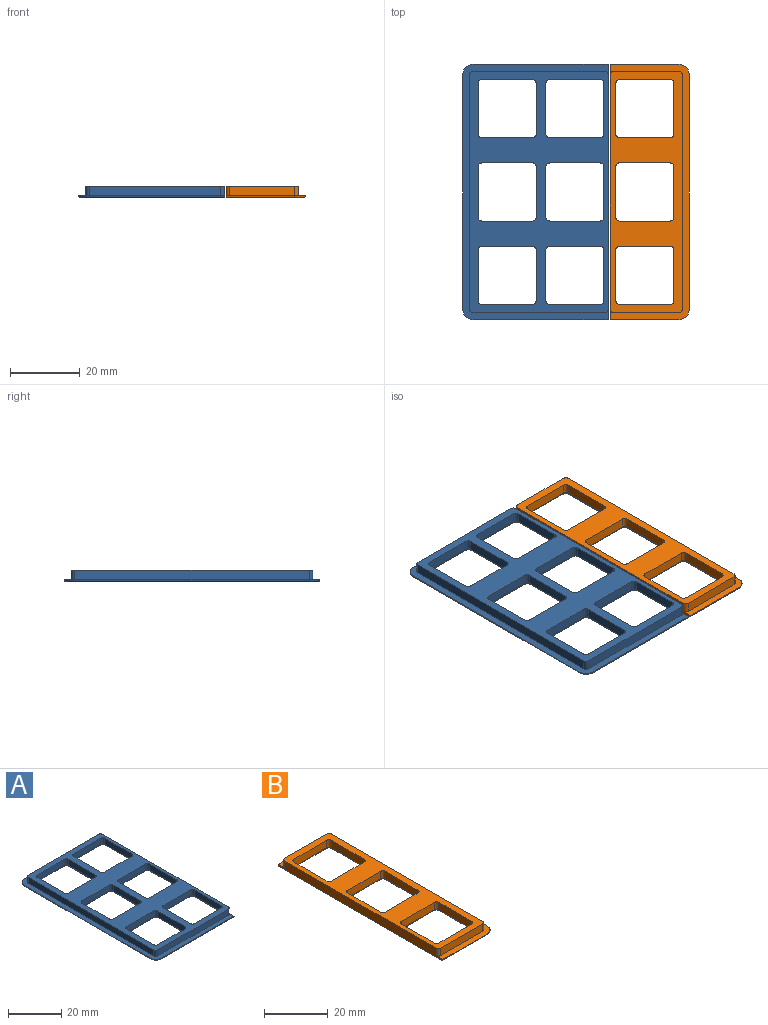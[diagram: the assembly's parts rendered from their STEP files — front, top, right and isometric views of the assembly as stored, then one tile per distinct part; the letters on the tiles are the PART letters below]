
ASSEMBLY  parts=2 mates=1
PART A: 112 faces, bbox 41.8x73.5x3.4 mm
  f0: plane 73x3.4mm, normal (1,0,0), area 231.2mm2, adj f1,f2,f30,f56,f57,f107,f111
  f1: plane 73x41.6mm, normal (0,0,1), area 301.4mm2, adj f0,f3,f4,f29,f55,f56,f57,f58
  f2: plane 71.8x41mm, normal (0,0,-1), area 1053.5mm2, adj f0,f59,f60,f61,f62,f63,f64,f65
  f3: plane 67x2.8mm, normal (-1,0,0), area 187.6mm2, adj f1,f30,f55,f58
  f4: plane 37.6x2.8mm, normal (0,-1,0), area 105.3mm2, adj f1,f30,f55,f56
  f5: plane 14.6x2.8mm, normal (1,0,0), area 40.9mm2, adj f30,f51,f54,f59
  f6: plane 14.6x2.8mm, normal (0,-1,0), area 40.9mm2, adj f30,f51,f52,f62
  f7: plane 14.6x2.8mm, normal (-1,0,0), area 40.9mm2, adj f30,f52,f53,f66
  f8: plane 14.6x2.8mm, normal (1,0,0), area 40.9mm2, adj f30,f47,f50,f67
  f9: plane 14.6x2.8mm, normal (0,-1,0), area 40.9mm2, adj f30,f47,f48,f70
  f10: plane 14.6x2.8mm, normal (-1,0,0), area 40.9mm2, adj f30,f48,f49,f74
  f11: plane 14.6x2.8mm, normal (1,0,0), area 40.9mm2, adj f30,f43,f46,f75
  f12: plane 14.6x2.8mm, normal (0,-1,0), area 40.9mm2, adj f30,f43,f44,f78
  f13: plane 14.6x2.8mm, normal (-1,0,0), area 40.9mm2, adj f30,f44,f45,f82
  f14: plane 14.6x2.8mm, normal (1,0,0), area 40.9mm2, adj f30,f39,f42,f83
  f15: plane 14.6x2.8mm, normal (0,-1,0), area 40.9mm2, adj f30,f39,f40,f86
  f16: plane 14.6x2.8mm, normal (-1,0,0), area 40.9mm2, adj f30,f40,f41,f90
  f17: plane 14.6x2.8mm, normal (1,0,0), area 40.9mm2, adj f30,f35,f38,f91
  f18: plane 14.6x2.8mm, normal (0,-1,0), area 40.9mm2, adj f30,f35,f36,f94
  f19: plane 14.6x2.8mm, normal (-1,0,0), area 40.9mm2, adj f30,f36,f37,f98
  f20: plane 14.6x2.8mm, normal (1,0,0), area 40.9mm2, adj f30,f31,f34,f99
  f21: plane 14.6x2.8mm, normal (0,-1,0), area 40.9mm2, adj f30,f31,f32,f102
  f22: plane 14.6x2.8mm, normal (-1,0,0), area 40.9mm2, adj f30,f32,f33,f106
  f23: plane 14.6x2.8mm, normal (0,1,0), area 40.9mm2, adj f30,f53,f54,f63
  f24: plane 14.6x2.8mm, normal (0,1,0), area 40.9mm2, adj f30,f49,f50,f71
  f25: plane 14.6x2.8mm, normal (0,1,0), area 40.9mm2, adj f30,f45,f46,f79
  f26: plane 14.6x2.8mm, normal (0,1,0), area 40.9mm2, adj f30,f41,f42,f87
  f27: plane 14.6x2.8mm, normal (0,1,0), area 40.9mm2, adj f30,f37,f38,f95
  f28: plane 14.6x2.8mm, normal (0,1,0), area 40.9mm2, adj f30,f33,f34,f103
  f29: plane 37.6x2.8mm, normal (0,1,0), area 105.3mm2, adj f1,f30,f57,f58
  f30: plane 69x39.6mm, normal (0,0,1), area 1083.3mm2, adj f0,f3,f4,f5,f6,f7,f8,f9
  f31: cylinder r=1mm len=2.8mm, axis (0,0,-1), area 4.4mm2, adj f20,f21,f30,f100
  f32: cylinder r=1mm len=2.8mm, axis (0,0,1), area 4.4mm2, adj f21,f22,f30,f104
  f33: cylinder r=1mm len=2.8mm, axis (0,0,-1), area 4.4mm2, adj f22,f28,f30,f105
  f34: cylinder r=1mm len=2.8mm, axis (0,0,1), area 4.4mm2, adj f20,f28,f30,f101
  f35: cylinder r=1mm len=2.8mm, axis (0,0,-1), area 4.4mm2, adj f17,f18,f30,f92
  f36: cylinder r=1mm len=2.8mm, axis (0,0,1), area 4.4mm2, adj f18,f19,f30,f96
  f37: cylinder r=1mm len=2.8mm, axis (0,0,-1), area 4.4mm2, adj f19,f27,f30,f97
  f38: cylinder r=1mm len=2.8mm, axis (0,0,1), area 4.4mm2, adj f17,f27,f30,f93
  f39: cylinder r=1mm len=2.8mm, axis (0,0,-1), area 4.4mm2, adj f14,f15,f30,f84
  f40: cylinder r=1mm len=2.8mm, axis (0,0,1), area 4.4mm2, adj f15,f16,f30,f88
  f41: cylinder r=1mm len=2.8mm, axis (0,0,-1), area 4.4mm2, adj f16,f26,f30,f89
  f42: cylinder r=1mm len=2.8mm, axis (0,0,1), area 4.4mm2, adj f14,f26,f30,f85
  f43: cylinder r=1mm len=2.8mm, axis (0,0,-1), area 4.4mm2, adj f11,f12,f30,f76
  f44: cylinder r=1mm len=2.8mm, axis (0,0,1), area 4.4mm2, adj f12,f13,f30,f80
  f45: cylinder r=1mm len=2.8mm, axis (0,0,-1), area 4.4mm2, adj f13,f25,f30,f81
  f46: cylinder r=1mm len=2.8mm, axis (0,0,1), area 4.4mm2, adj f11,f25,f30,f77
  f47: cylinder r=1mm len=2.8mm, axis (0,0,-1), area 4.4mm2, adj f8,f9,f30,f68
  f48: cylinder r=1mm len=2.8mm, axis (0,0,1), area 4.4mm2, adj f9,f10,f30,f72
  f49: cylinder r=1mm len=2.8mm, axis (0,0,-1), area 4.4mm2, adj f10,f24,f30,f73
  f50: cylinder r=1mm len=2.8mm, axis (0,0,1), area 4.4mm2, adj f8,f24,f30,f69
  f51: cylinder r=1mm len=2.8mm, axis (0,0,-1), area 4.4mm2, adj f5,f6,f30,f60
  f52: cylinder r=1mm len=2.8mm, axis (0,0,1), area 4.4mm2, adj f6,f7,f30,f64
  f53: cylinder r=1mm len=2.8mm, axis (0,0,-1), area 4.4mm2, adj f7,f23,f30,f65
  f54: cylinder r=1mm len=2.8mm, axis (0,0,1), area 4.4mm2, adj f5,f23,f30,f61
  f55: cylinder r=1mm len=2.8mm, axis (0,0,-1), area 4.4mm2, adj f1,f3,f4,f30
  f56: cylinder r=1mm len=2.8mm, axis (0,0,-1), area 4.4mm2, adj f0,f1,f4,f30
  f57: cylinder r=1mm len=2.8mm, axis (0,0,1), area 4.4mm2, adj f0,f1,f29,f30
  f58: cylinder r=1mm len=2.8mm, axis (0,0,1), area 4.4mm2, adj f1,f3,f29,f30
  f59: cylinder r=0.6mm len=14.6mm, axis (0,1,0), area 13.8mm2, adj f2,f5,f60,f61
  f60: torus R=1.6mm, axis (0,0,1), area 1.8mm2, adj f2,f51,f59,f62
  f61: torus R=1.6mm, axis (0,0,1), area 1.8mm2, adj f2,f54,f59,f63
  f62: cylinder r=0.6mm len=14.6mm, axis (1,0,0), area 13.8mm2, adj f2,f6,f60,f64
  f63: cylinder r=0.6mm len=14.6mm, axis (-1,0,0), area 13.8mm2, adj f2,f23,f61,f65
  f64: torus R=1.6mm, axis (0,0,1), area 1.8mm2, adj f2,f52,f62,f66
  f65: torus R=1.6mm, axis (0,0,1), area 1.8mm2, adj f2,f53,f63,f66
  f66: cylinder r=0.6mm len=14.6mm, axis (0,-1,0), area 13.8mm2, adj f2,f7,f64,f65
  f67: cylinder r=0.6mm len=14.6mm, axis (0,1,0), area 13.8mm2, adj f2,f8,f68,f69
  f68: torus R=1.6mm, axis (0,0,1), area 1.8mm2, adj f2,f47,f67,f70
  f69: torus R=1.6mm, axis (0,0,1), area 1.8mm2, adj f2,f50,f67,f71
  f70: cylinder r=0.6mm len=14.6mm, axis (1,0,0), area 13.8mm2, adj f2,f9,f68,f72
  f71: cylinder r=0.6mm len=14.6mm, axis (-1,0,0), area 13.8mm2, adj f2,f24,f69,f73
  f72: torus R=1.6mm, axis (0,0,1), area 1.8mm2, adj f2,f48,f70,f74
  f73: torus R=1.6mm, axis (0,0,1), area 1.8mm2, adj f2,f49,f71,f74
  f74: cylinder r=0.6mm len=14.6mm, axis (0,-1,0), area 13.8mm2, adj f2,f10,f72,f73
  f75: cylinder r=0.6mm len=14.6mm, axis (0,1,0), area 13.8mm2, adj f2,f11,f76,f77
  f76: torus R=1.6mm, axis (0,0,1), area 1.8mm2, adj f2,f43,f75,f78
  f77: torus R=1.6mm, axis (0,0,1), area 1.8mm2, adj f2,f46,f75,f79
  f78: cylinder r=0.6mm len=14.6mm, axis (1,0,0), area 13.8mm2, adj f2,f12,f76,f80
  f79: cylinder r=0.6mm len=14.6mm, axis (-1,0,0), area 13.8mm2, adj f2,f25,f77,f81
  f80: torus R=1.6mm, axis (0,0,1), area 1.8mm2, adj f2,f44,f78,f82
  f81: torus R=1.6mm, axis (0,0,1), area 1.8mm2, adj f2,f45,f79,f82
  f82: cylinder r=0.6mm len=14.6mm, axis (0,-1,0), area 13.8mm2, adj f2,f13,f80,f81
  f83: cylinder r=0.6mm len=14.6mm, axis (0,1,0), area 13.8mm2, adj f2,f14,f84,f85
  f84: torus R=1.6mm, axis (0,0,1), area 1.8mm2, adj f2,f39,f83,f86
  f85: torus R=1.6mm, axis (0,0,1), area 1.8mm2, adj f2,f42,f83,f87
  f86: cylinder r=0.6mm len=14.6mm, axis (1,0,0), area 13.8mm2, adj f2,f15,f84,f88
  f87: cylinder r=0.6mm len=14.6mm, axis (-1,0,0), area 13.8mm2, adj f2,f26,f85,f89
  f88: torus R=1.6mm, axis (0,0,1), area 1.8mm2, adj f2,f40,f86,f90
  f89: torus R=1.6mm, axis (0,0,1), area 1.8mm2, adj f2,f41,f87,f90
  f90: cylinder r=0.6mm len=14.6mm, axis (0,-1,0), area 13.8mm2, adj f2,f16,f88,f89
  f91: cylinder r=0.6mm len=14.6mm, axis (0,1,0), area 13.8mm2, adj f2,f17,f92,f93
  f92: torus R=1.6mm, axis (0,0,1), area 1.8mm2, adj f2,f35,f91,f94
  f93: torus R=1.6mm, axis (0,0,1), area 1.8mm2, adj f2,f38,f91,f95
  f94: cylinder r=0.6mm len=14.6mm, axis (1,0,0), area 13.8mm2, adj f2,f18,f92,f96
  f95: cylinder r=0.6mm len=14.6mm, axis (-1,0,0), area 13.8mm2, adj f2,f27,f93,f97
  f96: torus R=1.6mm, axis (0,0,1), area 1.8mm2, adj f2,f36,f94,f98
  f97: torus R=1.6mm, axis (0,0,1), area 1.8mm2, adj f2,f37,f95,f98
  f98: cylinder r=0.6mm len=14.6mm, axis (0,-1,0), area 13.8mm2, adj f2,f19,f96,f97
  f99: cylinder r=0.6mm len=14.6mm, axis (0,1,0), area 13.8mm2, adj f2,f20,f100,f101
  f100: torus R=1.6mm, axis (0,0,1), area 1.8mm2, adj f2,f31,f99,f102
  f101: torus R=1.6mm, axis (0,0,1), area 1.8mm2, adj f2,f34,f99,f103
  f102: cylinder r=0.6mm len=14.6mm, axis (1,0,0), area 13.8mm2, adj f2,f21,f100,f104
  f103: cylinder r=0.6mm len=14.6mm, axis (-1,0,0), area 13.8mm2, adj f2,f28,f101,f105
  f104: torus R=1.6mm, axis (0,0,1), area 1.8mm2, adj f2,f32,f102,f106
  f105: torus R=1.6mm, axis (0,0,1), area 1.8mm2, adj f2,f33,f103,f106
  f106: cylinder r=0.6mm len=14.6mm, axis (0,-1,0), area 13.8mm2, adj f2,f22,f104,f105
  f107: cylinder r=0.6mm len=38.6mm, axis (1,0,0), area 36.4mm2, adj f0,f1,f2,f108
  f108: torus R=2.4mm, axis (0,0,1), area 4.1mm2, adj f1,f2,f107,f109
  f109: cylinder r=0.6mm len=67mm, axis (0,-1,0), area 63.1mm2, adj f1,f2,f108,f110
  f110: torus R=2.4mm, axis (0,0,1), area 4.1mm2, adj f1,f2,f109,f111
  f111: cylinder r=0.6mm len=38.6mm, axis (-1,0,0), area 36.4mm2, adj f0,f1,f2,f110
PART B: 64 faces, bbox 22.8x73.5x3.4 mm
  f0: plane 73x3.4mm, normal (-1,0,0), area 231.2mm2, adj f1,f2,f18,f31,f34,f59,f63
  f1: plane 73x22.6mm, normal (0,0,1), area 225.4mm2, adj f0,f3,f4,f17,f31,f32,f33,f34
  f2: plane 71.8x22mm, normal (0,0,-1), area 633.2mm2, adj f0,f35,f36,f37,f38,f39,f40,f41
  f3: plane 18.6x2.8mm, normal (0,-1,0), area 52.1mm2, adj f1,f18,f31,f32
  f4: plane 67x2.8mm, normal (1,0,0), area 187.6mm2, adj f1,f18,f32,f33
  f5: plane 14.6x2.8mm, normal (1,0,0), area 40.9mm2, adj f18,f27,f30,f42
  f6: plane 14.6x2.8mm, normal (0,-1,0), area 40.9mm2, adj f18,f27,f28,f38
  f7: plane 14.6x2.8mm, normal (-1,0,0), area 40.9mm2, adj f18,f28,f29,f35
  f8: plane 14.6x2.8mm, normal (1,0,0), area 40.9mm2, adj f18,f23,f26,f50
  f9: plane 14.6x2.8mm, normal (0,-1,0), area 40.9mm2, adj f18,f23,f24,f46
  f10: plane 14.6x2.8mm, normal (-1,0,0), area 40.9mm2, adj f18,f24,f25,f43
  f11: plane 14.6x2.8mm, normal (1,0,0), area 40.9mm2, adj f18,f19,f22,f58
  f12: plane 14.6x2.8mm, normal (0,-1,0), area 40.9mm2, adj f18,f19,f20,f54
  f13: plane 14.6x2.8mm, normal (-1,0,0), area 40.9mm2, adj f18,f20,f21,f51
  f14: plane 14.6x2.8mm, normal (0,1,0), area 40.9mm2, adj f18,f29,f30,f39
  f15: plane 14.6x2.8mm, normal (0,1,0), area 40.9mm2, adj f18,f25,f26,f47
  f16: plane 14.6x2.8mm, normal (0,1,0), area 40.9mm2, adj f18,f21,f22,f55
  f17: plane 18.6x2.8mm, normal (0,1,0), area 52.1mm2, adj f1,f18,f33,f34
  f18: plane 69x20.6mm, normal (0,0,1), area 596.4mm2, adj f0,f3,f4,f5,f6,f7,f8,f9
  f19: cylinder r=1mm len=2.8mm, axis (0,0,-1), area 4.4mm2, adj f11,f12,f18,f56
  f20: cylinder r=1mm len=2.8mm, axis (0,0,1), area 4.4mm2, adj f12,f13,f18,f52
  f21: cylinder r=1mm len=2.8mm, axis (0,0,-1), area 4.4mm2, adj f13,f16,f18,f53
  f22: cylinder r=1mm len=2.8mm, axis (0,0,1), area 4.4mm2, adj f11,f16,f18,f57
  f23: cylinder r=1mm len=2.8mm, axis (0,0,-1), area 4.4mm2, adj f8,f9,f18,f48
  f24: cylinder r=1mm len=2.8mm, axis (0,0,1), area 4.4mm2, adj f9,f10,f18,f44
  f25: cylinder r=1mm len=2.8mm, axis (0,0,-1), area 4.4mm2, adj f10,f15,f18,f45
  f26: cylinder r=1mm len=2.8mm, axis (0,0,1), area 4.4mm2, adj f8,f15,f18,f49
  f27: cylinder r=1mm len=2.8mm, axis (0,0,-1), area 4.4mm2, adj f5,f6,f18,f40
  f28: cylinder r=1mm len=2.8mm, axis (0,0,1), area 4.4mm2, adj f6,f7,f18,f36
  f29: cylinder r=1mm len=2.8mm, axis (0,0,-1), area 4.4mm2, adj f7,f14,f18,f37
  f30: cylinder r=1mm len=2.8mm, axis (0,0,1), area 4.4mm2, adj f5,f14,f18,f41
  f31: cylinder r=1mm len=2.8mm, axis (0,0,-1), area 4.4mm2, adj f0,f1,f3,f18
  f32: cylinder r=1mm len=2.8mm, axis (0,0,1), area 4.4mm2, adj f1,f3,f4,f18
  f33: cylinder r=1mm len=2.8mm, axis (0,0,-1), area 4.4mm2, adj f1,f4,f17,f18
  f34: cylinder r=1mm len=2.8mm, axis (0,0,1), area 4.4mm2, adj f0,f1,f17,f18
  f35: cylinder r=0.6mm len=14.6mm, axis (0,-1,0), area 13.8mm2, adj f2,f7,f36,f37
  f36: torus R=1.6mm, axis (0,0,1), area 1.8mm2, adj f2,f28,f35,f38
  f37: torus R=1.6mm, axis (0,0,1), area 1.8mm2, adj f2,f29,f35,f39
  f38: cylinder r=0.6mm len=14.6mm, axis (1,0,0), area 13.8mm2, adj f2,f6,f36,f40
  f39: cylinder r=0.6mm len=14.6mm, axis (-1,0,0), area 13.8mm2, adj f2,f14,f37,f41
  f40: torus R=1.6mm, axis (0,0,1), area 1.8mm2, adj f2,f27,f38,f42
  f41: torus R=1.6mm, axis (0,0,1), area 1.8mm2, adj f2,f30,f39,f42
  f42: cylinder r=0.6mm len=14.6mm, axis (0,1,0), area 13.8mm2, adj f2,f5,f40,f41
  f43: cylinder r=0.6mm len=14.6mm, axis (0,-1,0), area 13.8mm2, adj f2,f10,f44,f45
  f44: torus R=1.6mm, axis (0,0,1), area 1.8mm2, adj f2,f24,f43,f46
  f45: torus R=1.6mm, axis (0,0,1), area 1.8mm2, adj f2,f25,f43,f47
  f46: cylinder r=0.6mm len=14.6mm, axis (1,0,0), area 13.8mm2, adj f2,f9,f44,f48
  f47: cylinder r=0.6mm len=14.6mm, axis (-1,0,0), area 13.8mm2, adj f2,f15,f45,f49
  f48: torus R=1.6mm, axis (0,0,1), area 1.8mm2, adj f2,f23,f46,f50
  f49: torus R=1.6mm, axis (0,0,1), area 1.8mm2, adj f2,f26,f47,f50
  f50: cylinder r=0.6mm len=14.6mm, axis (0,1,0), area 13.8mm2, adj f2,f8,f48,f49
  f51: cylinder r=0.6mm len=14.6mm, axis (0,-1,0), area 13.8mm2, adj f2,f13,f52,f53
  f52: torus R=1.6mm, axis (0,0,1), area 1.8mm2, adj f2,f20,f51,f54
  f53: torus R=1.6mm, axis (0,0,1), area 1.8mm2, adj f2,f21,f51,f55
  f54: cylinder r=0.6mm len=14.6mm, axis (1,0,0), area 13.8mm2, adj f2,f12,f52,f56
  f55: cylinder r=0.6mm len=14.6mm, axis (-1,0,0), area 13.8mm2, adj f2,f16,f53,f57
  f56: torus R=1.6mm, axis (0,0,1), area 1.8mm2, adj f2,f19,f54,f58
  f57: torus R=1.6mm, axis (0,0,1), area 1.8mm2, adj f2,f22,f55,f58
  f58: cylinder r=0.6mm len=14.6mm, axis (0,1,0), area 13.8mm2, adj f2,f11,f56,f57
  f59: cylinder r=0.6mm len=19.6mm, axis (1,0,0), area 18.5mm2, adj f0,f1,f2,f60
  f60: torus R=2.4mm, axis (0,0,1), area 4.1mm2, adj f1,f2,f59,f61
  f61: cylinder r=0.6mm len=67mm, axis (0,1,0), area 63.1mm2, adj f1,f2,f60,f62
  f62: torus R=2.4mm, axis (0,0,1), area 4.1mm2, adj f1,f2,f61,f63
  f63: cylinder r=0.6mm len=19.6mm, axis (-1,0,0), area 18.5mm2, adj f0,f1,f2,f62
PLACE A t=(28.94,20.83,8.85)mm
PLACE B t=(-3.45,20.83,8.85)mm
MATE slider A.f0 <-> B.f0  axis (1,0,0) through (12.74,73.74,10.53)mm
